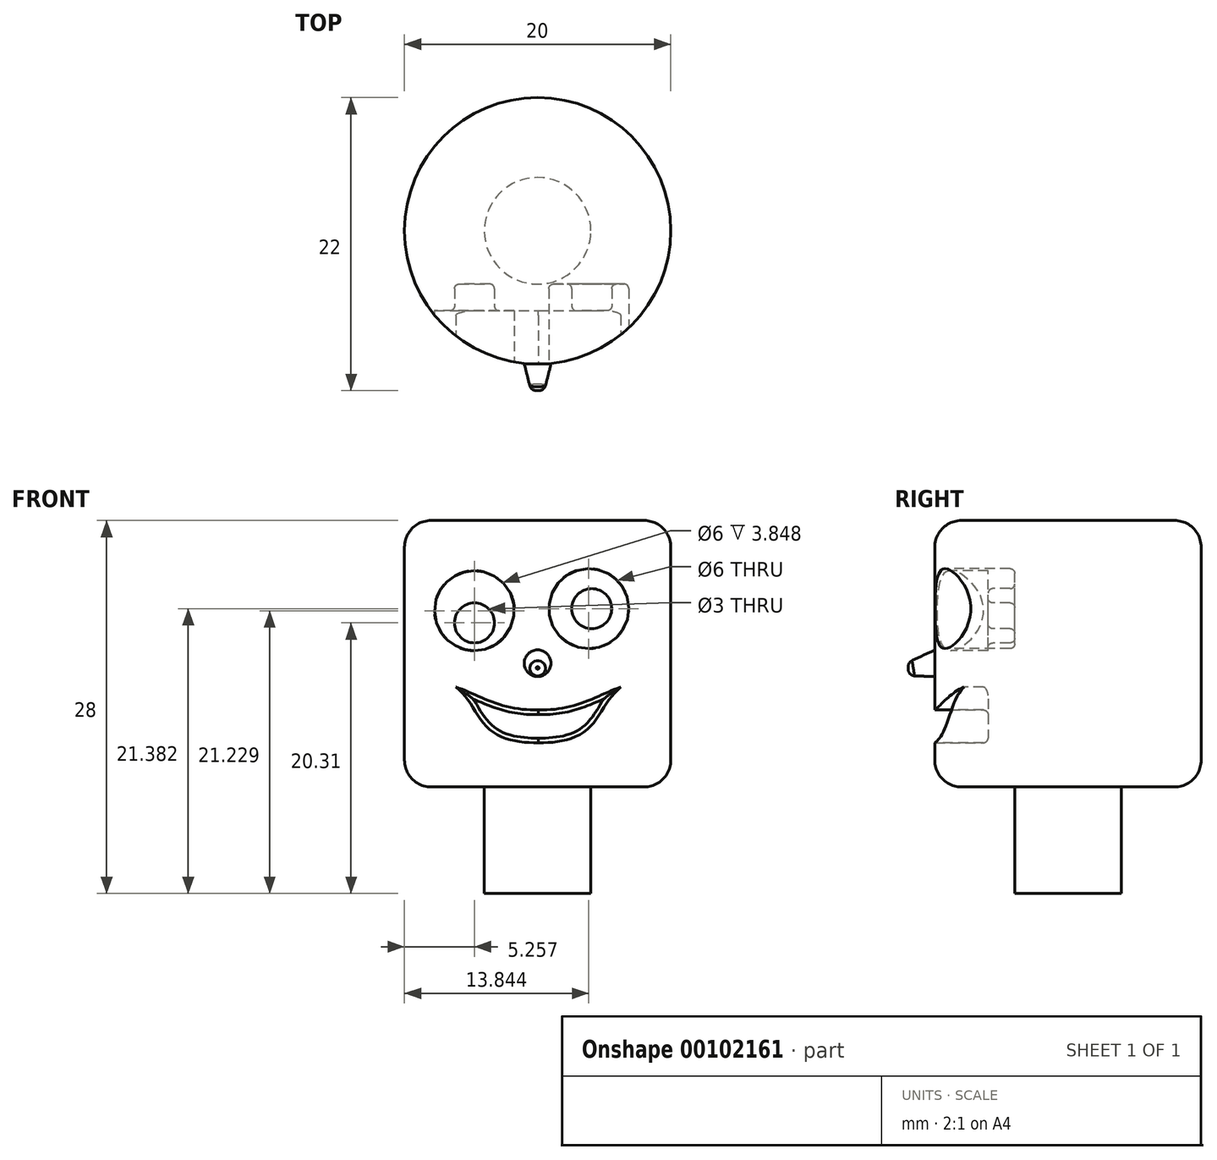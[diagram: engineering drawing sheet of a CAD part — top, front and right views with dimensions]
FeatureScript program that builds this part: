
annotation { "Feature Type Name" : "Feature", "Feature Type Description" : "" }
export const myFeature = defineFeature(function(context is Context, id is Id, definition is map)
    precondition{}
    {
        {
            var Q0;
            Q0=qCreatedBy(makeId("Top.planeOp"),FACE);
            var sketch = newSketch(context, id + "F0", { "sketchPlane" : qUnion([Q0])});
            skCircle(sketch, "E0", {"center": v(0, 0) * mm, "radius": 4 * mm});
            skSolve(sketch);
        }
        {
            var Q0;
            Q0=makeQuery(id+"F0.imprint","IMPRINT",FACE,{"disambiguationData":[TD([[makeQuery(id+"F0.imprint","IMPRINT",EDGE,{"derivedFrom":sQuery(id+"F0.wireOp",EDGE,"E0")}),1.0]])]});
            extrude(context, id + "F1", {"entities" : qUnion([Q0]), "depth" : 8 * mm});
        }
        {
            var Q0;
            Q0=makeQuery(id+"F1.opExtrude","CAP_FACE",FACE,{"disambiguationData":[OSD([sQuery(id+"F0.wireOp",EDGE,"E0")])],"isStart":false});
            cPlane(context, id + "F2", {"entities" : qUnion([Q0]), "cplaneType" : CPlaneType.OFFSET, "offset" : 0 * mm, "width" : 150 * mm, "height" : 150 * mm});
        }
        {
            var Q0;
            Q0=qCreatedBy(id+"F2.planeOp",FACE);
            var sketch = newSketch(context, id + "F3", { "sketchPlane" : qUnion([Q0])});
            skCircle(sketch, "E1", {"center": v(0, 0) * mm, "radius": 10 * mm});
            skSolve(sketch);
        }
        {
            var Q0;
            Q0 = qSketchRegion(id + "F3", true);
            extrude(context, id + "F4", {"entities" : qUnion([Q0]), "depth" : 20 * mm});
        }
        {
            var Q0;
            Q0=qCreatedBy(makeId("Front.planeOp"),FACE);
            cPlane(context, id + "F5", {"entities" : qUnion([Q0]), "cplaneType" : CPlaneType.OFFSET, "offset" : 10 * mm, "width" : 150 * mm, "height" : 150 * mm});
        }
        {
            var Q0;
            Q0=qCreatedBy(id+"F5.planeOp",FACE);
            var sketch = newSketch(context, id + "F6", { "sketchPlane" : qUnion([Q0])});
            skCircle(sketch, "E2", {"center": v(-4.74, 21.23) * mm, "radius": 3 * mm});
            skCircle(sketch, "E3", {"center": v(-4.74, 20.3) * mm, "radius": 1.5 * mm});
            skFitSpline(sketch, "E4", {"points": [v(0.06, 13.77) * mm, v(-6.14, 15.5) * mm], "startDerivative": vector(-8.63, -0.13) * mm, "endDerivative": vector(-5.7, 1.94) * mm});
            skFitSpline(sketch, "E5", {"points": [v(-6.14, 15.5) * mm, v(0.06, 11.31) * mm], "startDerivative": vector(6.08, -4.79) * mm, "endDerivative": vector(14.32, 0.13) * mm});
            skFitSpline(sketch, "E6.MirrorCS", {"points": [v(0.06, 13.77) * mm, v(6.26, 15.5) * mm], "startDerivative": vector(8.63, -0.13) * mm, "endDerivative": vector(5.7, 1.94) * mm});
            skFitSpline(sketch, "E7.MirrorCS", {"points": [v(6.26, 15.5) * mm, v(0.06, 11.31) * mm], "startDerivative": vector(-6.08, -4.79) * mm, "endDerivative": vector(-14.32, 0.13) * mm});
            skCircle(sketch, "E8.MirrorC", {"center": v(4.06, 21.38) * mm, "radius": 1.5 * mm});
            skCircle(sketch, "E9.MirrorC", {"center": v(3.84, 21.38) * mm, "radius": 3 * mm});
            skCircle(sketch, "E10", {"center": v(0, 17.28) * mm, "radius": 1 * mm});
            skSolve(sketch);
        }
        {
            var Q0;
            Q0=makeQuery(id+"F6.imprint","IMPRINT",FACE,{"disambiguationData":[TD([[makeQuery(id+"F6.imprint","IMPRINT",EDGE,{"derivedFrom":sQuery(id+"F6.wireOp",EDGE,"E2")}),1.0]])]});
            var Q1;
            Q1=makeQuery(id+"F6.imprint","IMPRINT",FACE,{"disambiguationData":[TD([[makeQuery(id+"F6.imprint","IMPRINT",EDGE,{"derivedFrom":sQuery(id+"F6.wireOp",EDGE,"E8.MirrorC")}),1.0]])]});
            var Q2;
            Q2=makeQuery(id+"F6.imprint","IMPRINT",FACE,{"disambiguationData":[TD([[makeQuery(id+"F6.imprint","IMPRINT",EDGE,{"derivedFrom":sQuery(id+"F6.wireOp",EDGE,"E4")}),1.0]])]});
            extrude(context, id + "F7", {"entities" : qUnion([Q0, Q1, Q2]), "operationType" : NewBodyOperationType.REMOVE, "oppositeDirection" : true, "depth" : 4 * mm});
        }
        {
            var Q0;
            Q0=makeQuery(id+"F6.imprint","IMPRINT",FACE,{"disambiguationData":[TD([[makeQuery(id+"F6.imprint","IMPRINT",EDGE,{"derivedFrom":sQuery(id+"F6.wireOp",EDGE,"E3")}),1.0]])]});
            var Q1;
            Q1=makeQuery(id+"F6.imprint","IMPRINT",FACE,{"disambiguationData":[TD([[makeQuery(id+"F6.imprint","IMPRINT",EDGE,{"derivedFrom":sQuery(id+"F6.wireOp",EDGE,"E8.MirrorC")}),-1.0]])]});
            extrude(context, id + "F8", {"entities" : qUnion([Q0, Q1]), "operationType" : NewBodyOperationType.REMOVE, "oppositeDirection" : true, "depth" : 6 * mm});
        }
        {
            var Q0;
            Q0=makeQuery(id+"F4.opExtrude","CAP_FACE",FACE,{"disambiguationData":[OSD([sQuery(id+"F3.wireOp",EDGE,"E1")])],"isStart":false});
            var Q1;
            Q1=makeQuery(id+"F4.opExtrude","CAP_FACE",FACE,{"disambiguationData":[OSD([sQuery(id+"F3.wireOp",EDGE,"E1")])],"isStart":true});
            fillet(context, id + "F9", {"entities" : qUnion([Q0, Q1]), "radius" : 2 * mm, "tangentPropagation" : true, "allowEdgeOverflow" : false});
        }
        {
            var Q0;
            Q0=makeQuery(id+"F8.boolean.opBoolean","COPY",FACE,{"derivedFrom":makeQuery(id+"F8.opExtrude","SWEPT_FACE",FACE,{"disambiguationData":[OSD([sQuery(id+"F6.wireOp",EDGE,"E3")])]})});
            var Q1;
            Q1=makeQuery(id+"F8.boolean.opBoolean","COPY",FACE,{"derivedFrom":makeQuery(id+"F8.opExtrude","CAP_FACE",FACE,{"disambiguationData":[OSD([sQuery(id+"F6.wireOp",EDGE,"E8.MirrorC")])],"isStart":false})});
            var Q2;
            Q2=makeQuery(id+"F8.boolean.opBoolean","COPY",FACE,{"derivedFrom":makeQuery(id+"F8.opExtrude","SWEPT_FACE",FACE,{"disambiguationData":[OSD([sQuery(id+"F6.wireOp",EDGE,"E8.MirrorC")])]})});
            var Q3;
            Q3=makeQuery(id+"F7.boolean.opBoolean","COPY",FACE,{"derivedFrom":makeQuery(id+"F7.opExtrude","CAP_FACE",FACE,{"disambiguationData":[OSD([sQuery(id+"F6.wireOp",EDGE,"E4"),sQuery(id+"F6.wireOp",EDGE,"E5"),sQuery(id+"F6.wireOp",EDGE,"E6.MirrorCS"),sQuery(id+"F6.wireOp",EDGE,"E7.MirrorCS")])],"isStart":false})});
            fillet(context, id + "F10", {"entities" : qUnion([Q0, Q1, Q2, Q3]), "radius" : .35 * mm, "tangentPropagation" : true, "allowEdgeOverflow" : false});
        }
        {
            var Q0;
            Q0=qCreatedBy(id+"F5.planeOp",FACE);
            cPlane(context, id + "F11", {"entities" : qUnion([Q0]), "cplaneType" : CPlaneType.OFFSET, "offset" : 2 * mm, "width" : 150 * mm, "height" : 150 * mm});
        }
        {
            var Q0;
            Q0=qCreatedBy(id+"F11.planeOp",FACE);
            var sketch = newSketch(context, id + "F12", { "sketchPlane" : qUnion([Q0])});
            skCircle(sketch, "E11", {"center": v(0, 16.85) * mm, "radius": 0.5 * mm});
            skSolve(sketch);
        }
        {
            var Q1;
            Q1=makeQuery(id+"F6.imprint","IMPRINT",FACE,{"disambiguationData":[TD([[makeQuery(id+"F6.imprint","IMPRINT",EDGE,{"derivedFrom":sQuery(id+"F6.wireOp",EDGE,"E10")}),1.0]])]});
            var Q2;
            Q2=makeQuery(id+"F12.imprint","IMPRINT",FACE,{"disambiguationData":[TD([[makeQuery(id+"F12.imprint","IMPRINT",EDGE,{"derivedFrom":sQuery(id+"F12.wireOp",EDGE,"E11")}),1.0]])]});
            loft(context, id + "F13", {"operationType" : NewBodyOperationType.ADD, "sheetProfilesArray" : [{ "sheetProfileEntities" : qUnion([Q1]) }, { "sheetProfileEntities" : qUnion([Q2]) }]});
        }
        {
            var Q0;
            Q0=makeQuery(id+"F13.opLoft","CAP_FACE",FACE,{"disambiguationData":[OSD([makeQuery(id+"F12.imprint","IMPRINT",FACE,{"disambiguationData":[TD([[makeQuery(id+"F12.imprint","IMPRINT",EDGE,{"derivedFrom":sQuery(id+"F12.wireOp",EDGE,"E11")}),1.0]])]})])],"isStart":true});
            fillet(context, id + "F14", {"entities" : qUnion([Q0]), "radius" : .5 * mm, "tangentPropagation" : true, "allowEdgeOverflow" : false});
        }
    });
